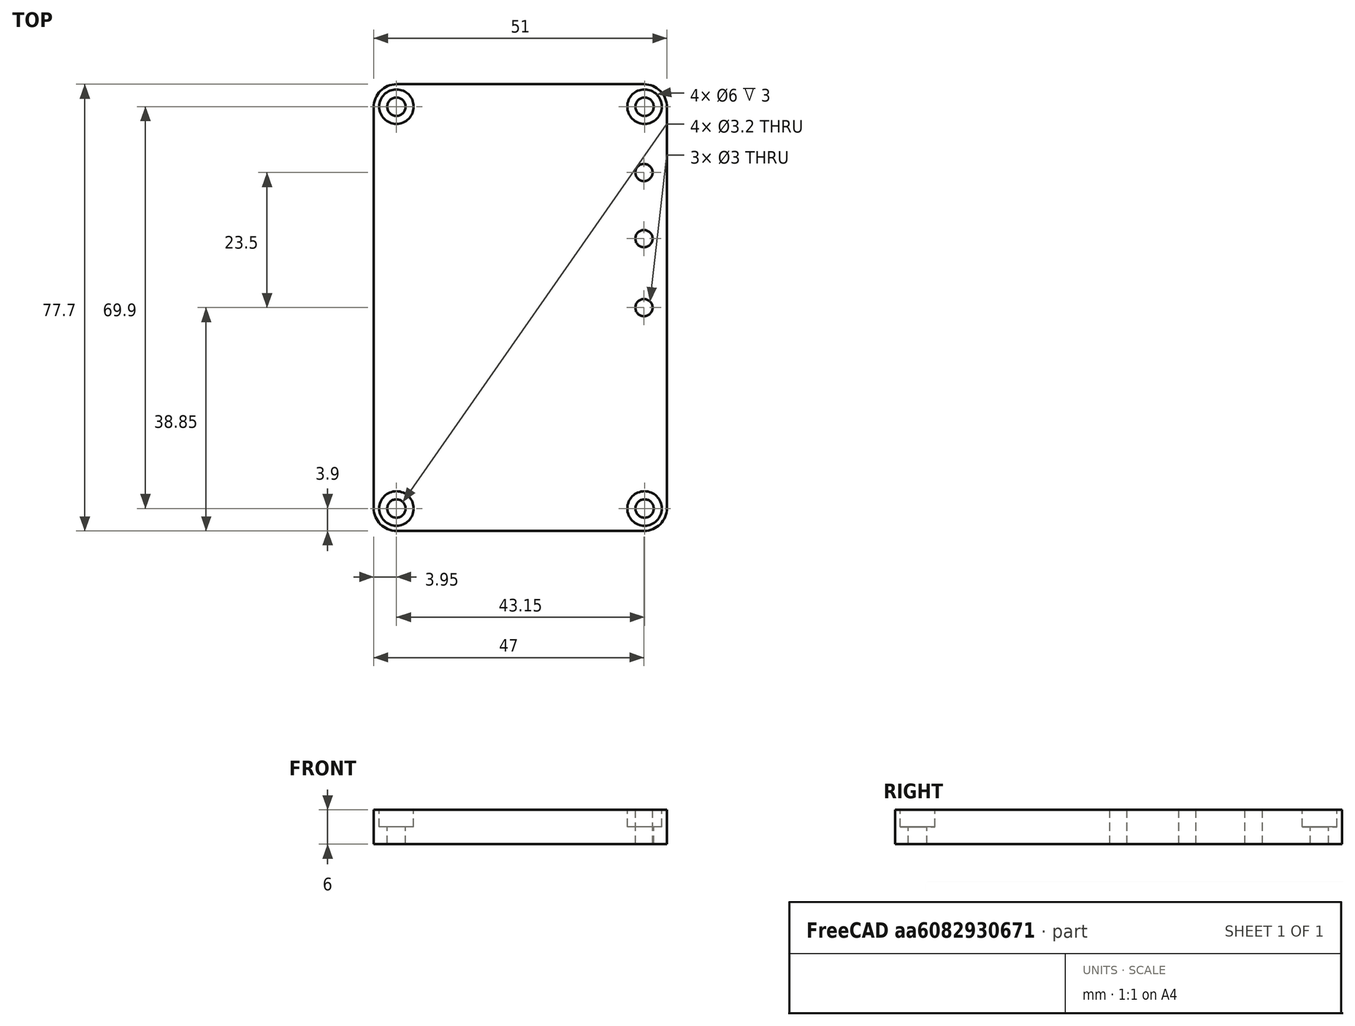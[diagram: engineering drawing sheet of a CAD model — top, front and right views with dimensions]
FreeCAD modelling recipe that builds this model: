
FCSTD DOCUMENT  (FreeCAD 0.18R16146 (Git))
Label: front-plate
License: All rights reserved
LicenseURL: http://en.wikipedia.org/wiki/All_rights_reserved
objects: Part::Cylinder×11, Part::Cut×7, Part::Fuse×4, Mesh::Feature×1, Part::Box×1, Part::Fillet×1, App::DocumentObjectGroup×1
note: 24 computed .brp shape members not serialized (recipe doc carries the construction recipe); baked Part::Feature solids carry a one-line shape summary decoded from their .brp

FEATURE [Mesh::Feature] custom_arduino_rtc_temperature_humidity  label="custom-arduino-rtc-temperature-humidity"
FEATURE [Part::Box] Box  label="Würfel"
  AttacherType = Attacher::AttachEngine3D
  Height = 6
  Length = 51
  Placement = pos=(-25.5,-38.85,0) rot=(0,0,1;0rad)
  Width = 77.7
FEATURE [Part::Fillet] Fillet
  Base = -> Box
  Edges = 4 edges r=4: [Edge1,Edge3,Edge5,Edge7]
FEATURE [Part::Cylinder] Cylinder  label="Zylinder"
  Angle = 360
  AttacherType = Attacher::AttachEngine3D
  Height = 8
  Placement = pos=(-21.55,34.95,-1.95) rot=(0,0,1;0rad)
  Radius = 1.6
FEATURE [Part::Cylinder] Cylinder001  label="Zylinder001"
  Angle = 360
  AttacherType = Attacher::AttachEngine3D
  Height = 3
  Placement = pos=(-21.55,34.95,3) rot=(0,0,1;0rad)
  Radius = 3
FEATURE [Part::Fuse] Fusion  label="Hole1"
  Base = -> Cylinder
  Refine = true
  Tool = -> Cylinder001
FEATURE [Part::Cylinder] Cylinder002  label="Zylinder002"
  Angle = 360
  AttacherType = Attacher::AttachEngine3D
  Height = 8
  Placement = pos=(-21.55,34.95,-1.95) rot=(0,0,1;0rad)
  Radius = 1.6
FEATURE [Part::Cylinder] Cylinder003  label="Zylinder003"
  Angle = 360
  AttacherType = Attacher::AttachEngine3D
  Height = 3
  Placement = pos=(-21.55,34.95,3) rot=(0,0,1;0rad)
  Radius = 3
FEATURE [Part::Fuse] Fusion001  label="Hole2"
  Base = -> Cylinder002
  Placement = pos=(0,-69.9,0) rot=(0,0,1;0rad)
  Refine = true
  Tool = -> Cylinder003
FEATURE [Part::Cylinder] Cylinder004  label="Zylinder004"
  Angle = 360
  AttacherType = Attacher::AttachEngine3D
  Height = 3
  Placement = pos=(-21.55,34.95,3) rot=(0,0,1;0rad)
  Radius = 3
FEATURE [Part::Cylinder] Cylinder005  label="Zylinder005"
  Angle = 360
  AttacherType = Attacher::AttachEngine3D
  Height = 8
  Placement = pos=(-21.55,34.95,-1.95) rot=(0,0,1;0rad)
  Radius = 1.6
FEATURE [Part::Fuse] Fusion002  label="Hole3"
  Base = -> Cylinder005
  Placement = pos=(43.15,-69.9,0) rot=(0,0,1;0rad)
  Refine = true
  Tool = -> Cylinder004
FEATURE [Part::Cylinder] Cylinder006  label="Zylinder006"
  Angle = 360
  AttacherType = Attacher::AttachEngine3D
  Height = 8
  Placement = pos=(-21.55,34.95,-1.95) rot=(0,0,1;0rad)
  Radius = 1.6
FEATURE [Part::Cylinder] Cylinder007  label="Zylinder007"
  Angle = 360
  AttacherType = Attacher::AttachEngine3D
  Height = 3
  Placement = pos=(-21.55,34.95,3) rot=(0,0,1;0rad)
  Radius = 3
FEATURE [Part::Fuse] Fusion003  label="Hole4"
  Base = -> Cylinder006
  Placement = pos=(43.15,0,0) rot=(0,0,1;0rad)
  Refine = true
  Tool = -> Cylinder007
FEATURE [Part::Cut] Cut
  Base = -> Fillet
  Refine = true
  Tool = -> Fusion
FEATURE [Part::Cut] Cut001
  Base = -> Cut
  Refine = true
  Tool = -> Fusion001
FEATURE [Part::Cut] Cut002
  Base = -> Cut001
  Refine = true
  Tool = -> Fusion002
FEATURE [Part::Cut] Cut003
  Base = -> Cut002
  Placement = pos=(0,0,10.6) rot=(0,0,1;0rad)
  Refine = true
  Tool = -> Fusion003
FEATURE [Part::Cylinder] Cylinder008  label="Zylinder008"
  Angle = 360
  AttacherType = Attacher::AttachEngine3D
  Height = 26
  Placement = pos=(21.5,23.5,0) rot=(0,0,1;0rad)
  Radius = 1.5
FEATURE [Part::Cylinder] Cylinder009  label="Zylinder009"
  Angle = 360
  AttacherType = Attacher::AttachEngine3D
  Height = 26
  Placement = pos=(21.5,12,0) rot=(0,0,1;0rad)
  Radius = 1.5
FEATURE [Part::Cylinder] Cylinder010  label="Zylinder010"
  Angle = 360
  AttacherType = Attacher::AttachEngine3D
  Height = 26
  Placement = pos=(21.5,0,0) rot=(0,0,1;0rad)
  Radius = 1.5
FEATURE [Part::Cut] Cut004
  Base = -> Cut003
  Refine = true
  Tool = -> Cylinder009
FEATURE [Part::Cut] Cut005
  Base = -> Cut004
  Refine = true
  Tool = -> Cylinder010
FEATURE [Part::Cut] Cut006
  Base = -> Cut005
  Refine = true
  Tool = -> Cylinder008
FEATURE [App::DocumentObjectGroup] Gruppe  label="Button Löcher"
  Group = -> [Cut006]
